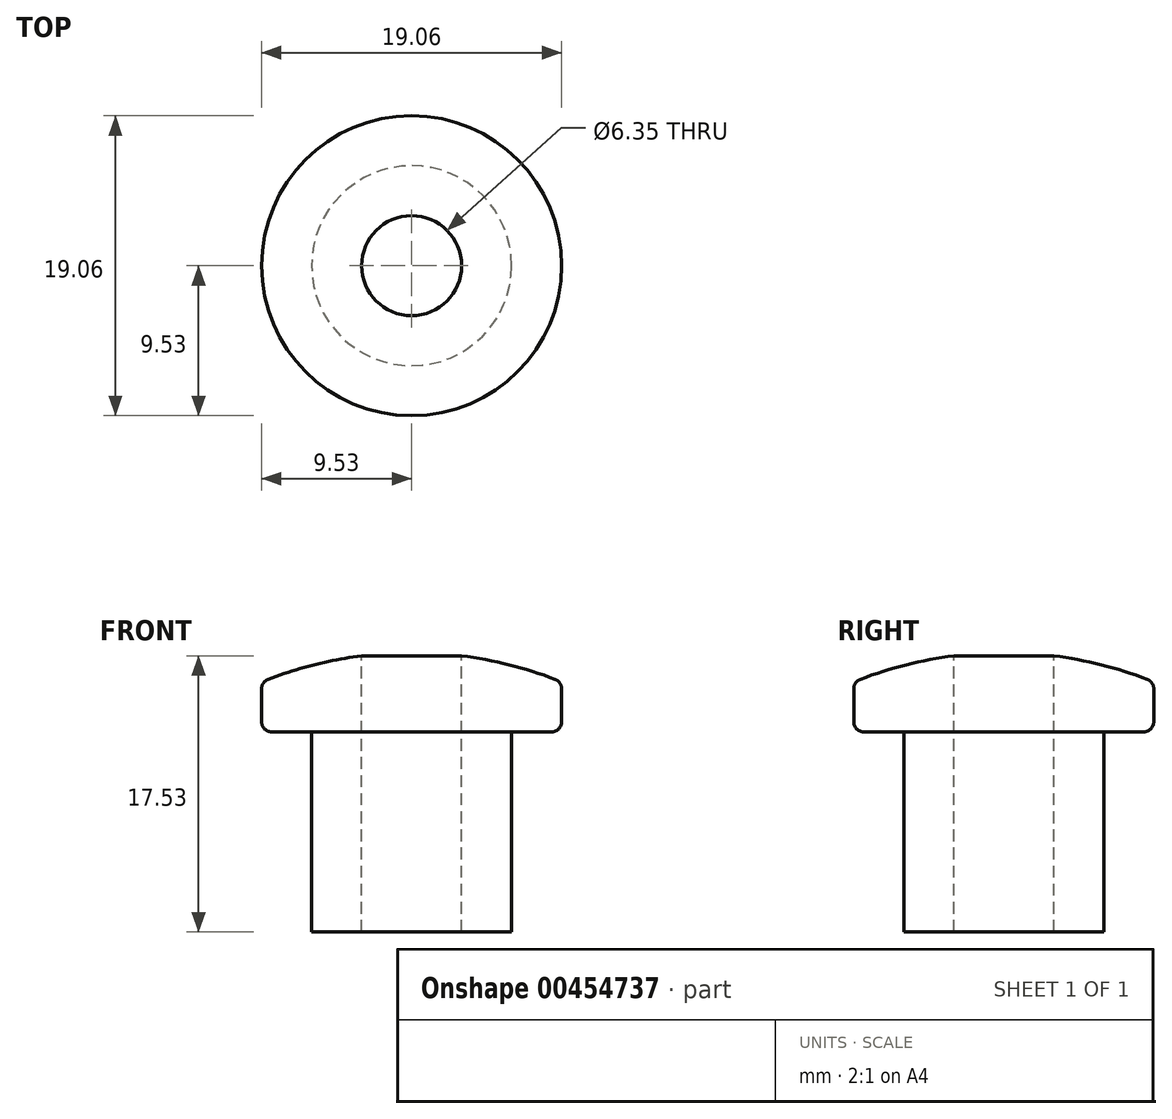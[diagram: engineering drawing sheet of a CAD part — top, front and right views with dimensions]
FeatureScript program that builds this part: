
annotation { "Feature Type Name" : "Feature", "Feature Type Description" : "" }
export const myFeature = defineFeature(function(context is Context, id is Id, definition is map)
    precondition{}
    {
        {
            var Q0;
            Q0=qCreatedBy(makeId("Front.planeOp"),FACE);
            var sketch = newSketch(context, id + "F0", { "sketchPlane" : qUnion([Q0])});
            skLineSegment(sketch, "E0", {"start": v(0, 0) * mm, "end": v(-6.35, 0) * mm});
            skLineSegment(sketch, "E1", {"start": v(-6.35, 0) * mm, "end": v(-6.35, 12.7) * mm});
            skLineSegment(sketch, "E2", {"start": v(-6.35, 12.7) * mm, "end": v(-9.53, 12.7) * mm});
            skLineSegment(sketch, "E3", {"start": v(-9.53, 12.7) * mm, "end": v(-9.53, 15.88) * mm});
            skLineSegment(sketch, "E4", {"start": v(0, 0) * mm, "end": v(0, 17.6) * mm});
            skArc(sketch, "E5", {"start": v(-2.54, 17.6) * mm, "mid": v(-6.1, 16.99) * mm, "end": v(-9.53, 15.88) * mm});
            skArc(sketch, "E6", {"start": v(-9.53, 15.87) * mm, "mid": v(4.85, -32.6) * mm, "end": v(0, 17.73) * mm, "construction": true});
            skLineSegment(sketch, "E7", {"start": v(0, 17.6) * mm, "end": v(-2.54, 17.6) * mm});
            skLineSegment(sketch, "E8", {"start": v(0, 17.6) * mm, "end": v(0, 17.73) * mm, "construction": true});
            skSolve(sketch);
        }
        {
            var Q0;
            Q0=makeQuery(id+"F0.imprint","IMPRINT",FACE,{"disambiguationData":[TD([[makeQuery(id+"F0.imprint","IMPRINT",EDGE,{"derivedFrom":sQuery(id+"F0.wireOp",EDGE,"E0")}),-1.0]])]});
            var Q1;
            Q1=sQuery(id+"F0.wireOp",EDGE,"E4");
            revolve(context, id + "F1", {"entities" : qUnion([Q0]), "axis" : qUnion([Q1]), "revolveType" : RevolveType.FULL});
        }
        {
            var Q0;
            Q0=makeQuery(id+"F1.opRevolve","SWEPT_FACE",FACE,{"disambiguationData":[OSD([sQuery(id+"F0.wireOp",EDGE,"E7")])]});
            var sketch = newSketch(context, id + "F2", { "sketchPlane" : qUnion([Q0])});
            skCircle(sketch, "E9.0", {"center": v(0, 0) * mm, "radius": 2.54 * mm});
            skSolve(sketch);
        }
        {
            var Q0;
            Q0=sQuery(id+"F2.wireOp",VERTEX,"E9.0.center");
            var Q1;
            Q1=makeQuery(id+"F1.opRevolve","SWEPT_BODY",BODY,{"disambiguationData":[OSD([sQuery(id+"F0.wireOp",EDGE,"E0"),sQuery(id+"F0.wireOp",EDGE,"E1"),sQuery(id+"F0.wireOp",EDGE,"E2"),sQuery(id+"F0.wireOp",EDGE,"E3"),sQuery(id+"F0.wireOp",EDGE,"E4"),sQuery(id+"F0.wireOp",EDGE,"E5"),sQuery(id+"F0.wireOp",EDGE,"E7")])]});
            hole(context, id + "F3", {"style" : HoleStyle.SIMPLE, "endStyle" : HoleEndStyle.THROUGH, "holeDiameter" : 6.35 * mm, "majorDiameter" : 6.35 * mm, "isTappedThrough" : true, "tappedDepth" : 12.7 * mm, "tapClearance" : 3, "locations" : qUnion([Q0]), "scope" : qUnion([Q1])});
        }
        {
            var Q0;
            Q0=makeQuery(id+"F1.opRevolve","SWEPT_EDGE",EDGE,{"disambiguationData":[OSD([sQuery(id+"F0.wireOp",EDGE,"E2"),sQuery(id+"F0.wireOp",EDGE,"E3")])]});
            var Q1;
            Q1=makeQuery(id+"F1.opRevolve","SWEPT_EDGE",EDGE,{"disambiguationData":[OSD([sQuery(id+"F0.wireOp",EDGE,"E3"),sQuery(id+"F0.wireOp",EDGE,"E5")])]});
            fillet(context, id + "F4", {"entities" : qUnion([Q0, Q1]), "radius" : 0.64 * mm, "tangentPropagation" : true, "allowEdgeOverflow" : false});
        }
    });
